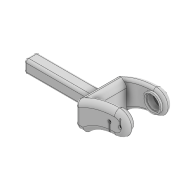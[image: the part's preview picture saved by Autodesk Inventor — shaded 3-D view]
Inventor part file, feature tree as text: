
AUTODESK INVENTOR PART (.ipt)
format: ipt  version: 2020 (Build 240168000, 168)  size: 456,192 bytes
history: native  units: mm
features: fillet x9, extrude x8, sketch x8, mirror x2, projected_geometry x1, plane x1
ambient origin geometry x8: Origin, YZ Plane, XZ Plane, XY Plane, X Axis, Y Axis, Z Axis, Center Point
bodies: Solid1 (feature_tree)
feature tree (29):
  extrude  "Extrusion1"  Depth=13.5mm
  extrude  "Extrusion2"  Depth=9.0mm
  extrude  "Extrusion3"  Depth=10.0mm
  fillet  "Fillet3"  Radius=9.0mm
  fillet  "Fillet4"  Radius=10.0mm
  extrude  "Extrusion4"  Depth=2.0mm
  extrude  "Extrusion5"  Depth=5.0mm
  extrude  "Extrusion6"  Depth=2.0mm TaperAngle=0.0deg
  fillet  "Fillet5"  Radius=6.0mm
  fillet  "Fillet6"  Radius=15.0mm
  extrude  "Extrusion7"  Depth=2.5mm
  fillet  "Fillet7"  Radius=26.0mm
  mirror  "Mirror1"
  extrude  "Extrusion8"  Depth=2.0mm
  mirror  "Mirror2"
  fillet  "Fillet8"  Radius=2.0mm
  fillet  "Fillet9"  Radius=5.2mm
  fillet  "Fillet10"  Radius=2.4mm
  fillet  "Fillet11"  Radius=5.2mm
  sketch  "Sketch1"  dims[d0=46.0mm d1=13.5mm]
  sketch  "Sketch2"  dims[d2=18.0mm d3=0.0mm d4=9.0mm]
  sketch  "Sketch3"  dims[d5=4.5mm d6=5.0mm d7=9.0mm d8=10.0mm]
  sketch  "Sketch4"  dims[d9=5.0mm d10=2.0mm]
  sketch  "Sketch5"  dims[d11=4.0mm d12=5.0mm]
  sketch  "Sketch6"  dims[d13=2.0mm d14=18.0mm d15=0.0mm d17=6.0mm d18=15.0mm]
  projected_geometry  "Projected Loop1"
  sketch  "Sketch7"  dims[d19=12.0mm d20=2.5mm d21=26.0mm]
  plane  "Work Plane1"
  sketch  "Sketch8"  dims[d22=18.0mm d23=0.0mm d25=2.0mm d26=2.0mm d27=5.2mm d28=2.4mm d29=0.0mm d30=5.2mm d31=2.4mm d32=0.0mm d33=2.0mm d34=20.4mm d35=1.2mm d36=0.0mm d37=0.0mm d38=1.0mm d39=1.0mm d40=7.0mm d41=6.0mm d42=1.0mm d43=0.0mm d44=0.5mm d45=0.0mm d46=0.25mm d47=0.2mm d48=0.24mm d49=0.0mm d50=0.25mm d51=5.0mm d52=4.0mm d53=2.0mm d54=1.75mm d55=1.0mm d56=1.0mm]
